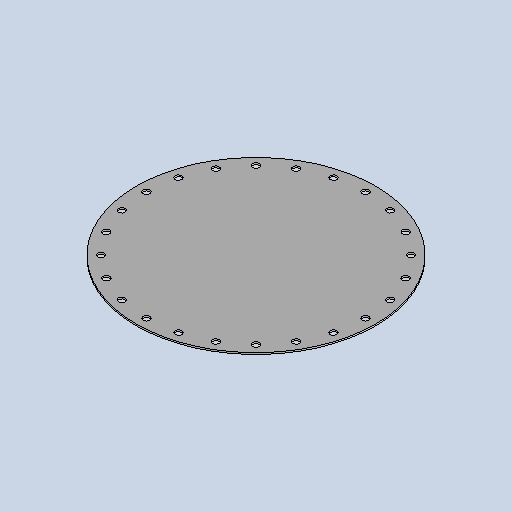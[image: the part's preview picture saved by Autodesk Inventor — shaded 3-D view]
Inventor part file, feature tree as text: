
AUTODESK INVENTOR PART (.ipt)
format: ipt  version: 2025 (Build 290162010, 162A)  size: 161,792 bytes
history: native  units: mm
features: sketch x2, other x2, sheet_metal_op x1, extrude x1, pattern_circular x1
ambient origin geometry x8: Origin, YZ Plane, XZ Plane, XY Plane, X Axis, Y Axis, Z Axis, Center Point
bodies: Solid1 (feature_tree)
feature tree (7):
  sheet_metal_op  "Face1"
  extrude  "Extrusion1"  Depth=4.0mm
  pattern_circular  "Circular Pattern1"  Count=55  [1 undecoded]
  sketch  "Sketch1"  dims[d0=600.0mm d1=4.0mm d2=550.0mm]
  other  "Plate1"
  sketch  "Sketch2"  dims[d3=17.0mm d4=0.0mm d5=0.0mm d6=240.0mm d7=360.0deg]
  other  "Definition1"
note: 1 required parameter value undecoded (feature->parameter linkage not recoverable at this tier; creation-order binding heuristic only, values carry confidence <= 0.55)
